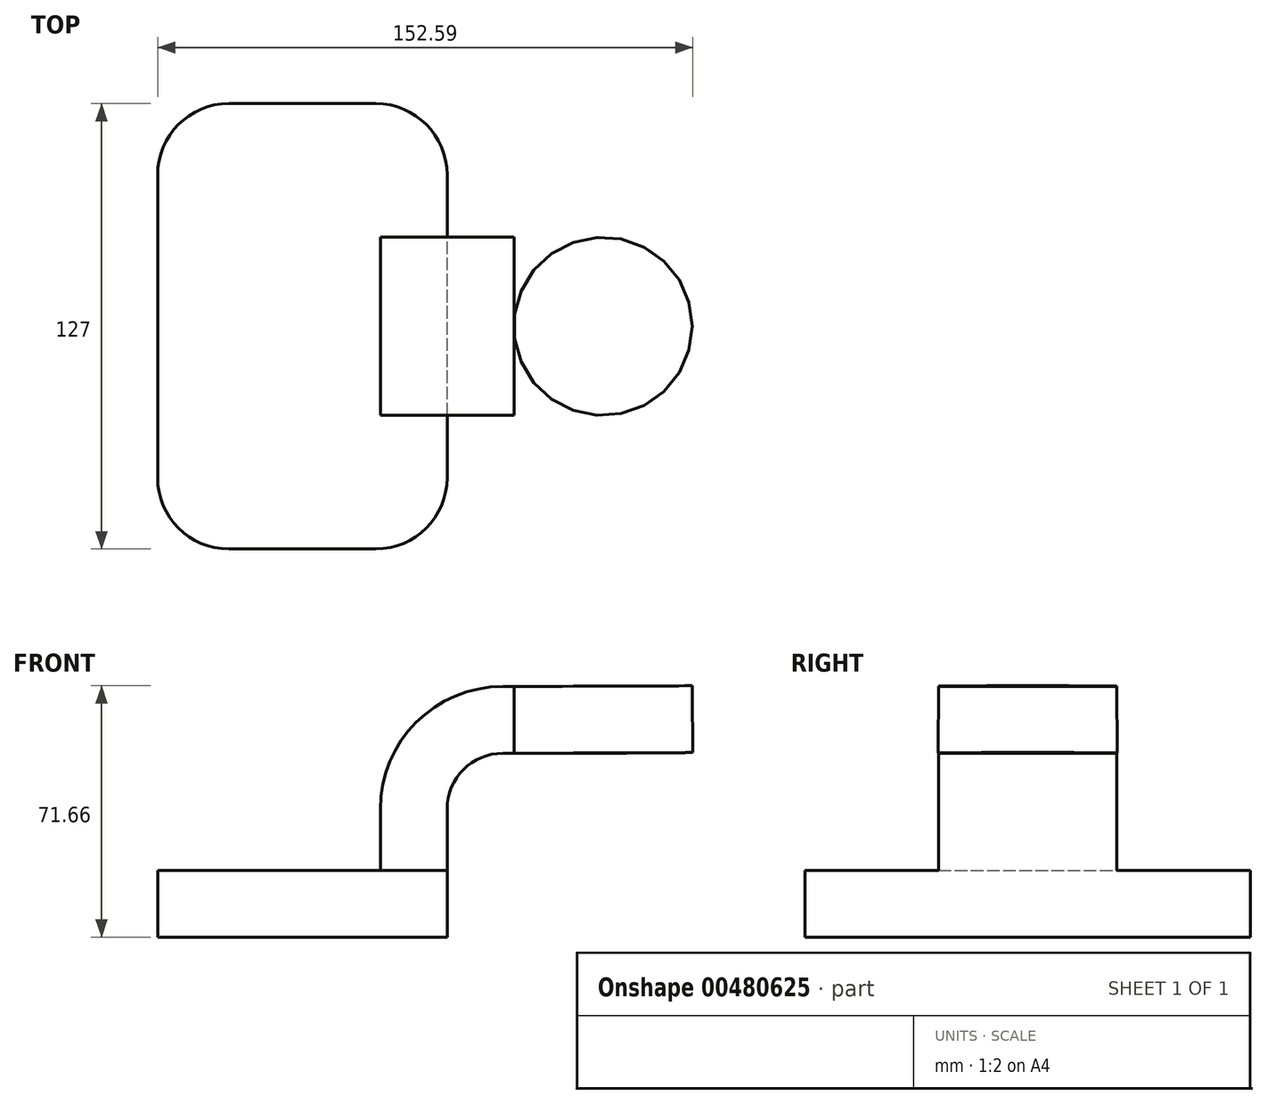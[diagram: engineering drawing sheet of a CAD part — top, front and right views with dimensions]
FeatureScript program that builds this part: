
annotation { "Feature Type Name" : "Feature", "Feature Type Description" : "" }
export const myFeature = defineFeature(function(context is Context, id is Id, definition is map)
    precondition{}
    {
        {
            var Q0;
            Q0=qCreatedBy(makeId("Front.planeOp"),FACE);
            var sketch = newSketch(context, id + "F0", { "sketchPlane" : qUnion([Q0])});
            skLineSegment(sketch, "E0.bottom", {"start": v(-41.28, 9.52) * mm, "end": v(41.27, 9.53) * mm});
            skLineSegment(sketch, "E0.top", {"start": v(-41.28, -9.52) * mm, "end": v(41.28, -9.52) * mm});
            skLineSegment(sketch, "E0.left", {"start": v(-41.28, 9.52) * mm, "end": v(-41.28, -9.53) * mm});
            skLineSegment(sketch, "E0.right", {"start": v(41.27, 9.53) * mm, "end": v(41.28, -9.52) * mm});
            skPoint(sketch, "E0.middle", {"position": v(0, 0) * mm});
            skLineSegment(sketch, "E1.bottom", {"start": v(60.32, 38.1) * mm, "end": v(111.12, 38.1) * mm});
            skLineSegment(sketch, "E1.top", {"start": v(60.32, 66.68) * mm, "end": v(111.12, 66.68) * mm});
            skLineSegment(sketch, "E1.left", {"start": v(60.32, 38.1) * mm, "end": v(60.32, 66.68) * mm});
            skLineSegment(sketch, "E1.right", {"start": v(111.12, 38.1) * mm, "end": v(111.12, 66.68) * mm});
            skPoint(sketch, "E1.middle", {"position": v(85.72, 52.39) * mm});
            skLineSegment(sketch, "E2", {"start": v(41.27, 9.53) * mm, "end": v(41.27, 27) * mm});
            skArc(sketch, "E3", {"start": v(41.27, 27) * mm, "mid": v(45.92, 38.23) * mm, "end": v(57.15, 42.88) * mm});
            skLineSegment(sketch, "E4", {"start": v(57.15, 42.88) * mm, "end": v(85.82, 42.88) * mm});
            skLineSegment(sketch, "E5.0", {"start": v(57.15, 61.93) * mm, "end": v(85.74, 61.93) * mm});
            skArc(sketch, "E5.1", {"start": v(22.22, 27) * mm, "mid": v(32.45, 51.7) * mm, "end": v(57.15, 61.93) * mm});
            skLineSegment(sketch, "E5.2", {"start": v(22.22, 9.53) * mm, "end": v(22.22, 27) * mm});
            skFitSpline(sketch, "E6", {"points": [v(-41.28, 9.52) * mm, v(57.15, 61.93) * mm], "startDerivative": vector(24.3, 107.09) * mm, "endDerivative": vector(112.36, -40.67) * mm});
            skLineSegment(sketch, "E7", {"start": v(85.72, 66.68) * mm, "end": v(85.74, 61.93) * mm});
            skLineSegment(sketch, "E8", {"start": v(85.74, 61.93) * mm, "end": v(85.82, 42.88) * mm});
            skLineSegment(sketch, "E9", {"start": v(85.82, 42.88) * mm, "end": v(85.82, 38.1) * mm});
            skSolve(sketch);
        }
        {
            var Q0;
            Q0=makeQuery(id+"F0.imprint","IMPRINT",FACE,{"disambiguationData":[TD([[makeQuery(id+"F0.imprint","IMPRINT",EDGE,{"derivedFrom":sQuery(id+"F0.wireOp",EDGE,"E0.top")}),1.0]])]});
            extrude(context, id + "F1", {"entities" : qUnion([Q0]), "endBound" : BoundingType.SYMMETRIC, "depth" : 127 * mm});
        }
        {
            var Q0;
            {var subQ1=sQuery(id+"F0.wireOp",EDGE,"E2");Q0=makeQuery(id+"F0.imprint","IMPRINT",FACE,{"disambiguationData":[TD([[makeQuery(id+"F0.imprint","IMPRINT",EDGE,{"derivedFrom":subQ1}),1.0]])]});}
            var Q1;
            {var subQ5=sQuery(id+"F0.wireOp",EDGE,"tLnTp5P4-59iU-ndsa-wNFi-t6ebqTft85pR");Q1=makeQuery(id+"F0.imprint","IMPRINT",FACE,{"disambiguationData":[TD([[makeQuery(id+"F0.imprint","IMPRINT",EDGE,{"derivedFrom":subQ5}),1.0]])]});}
            extrude(context, id + "F2", {"entities" : qUnion([Q0, Q1]), "operationType" : NewBodyOperationType.ADD, "endBound" : BoundingType.SYMMETRIC, "depth" : 50.8 * mm});
        }
        {
            var Q0;
            Q0=makeQuery(id+"F0.imprint","IMPRINT",FACE,{"disambiguationData":[TD([[makeQuery(id+"F0.imprint","IMPRINT",EDGE,{"derivedFrom":sQuery(id+"F0.wireOp",EDGE,"E5.1")}),1.0]])]});
            extrude(context, id + "F3", {"entities" : qUnion([Q0]), "operationType" : NewBodyOperationType.ADD, "endBound" : BoundingType.SYMMETRIC, "depth" : 15.88 * mm});
        }
        {
            var Q0;
            {var subQ5=sQuery(id+"F0.wireOp",EDGE,"E8");Q0=makeQuery(id+"F0.imprint","IMPRINT",FACE,{"disambiguationData":[TD([[makeQuery(id+"F0.imprint","IMPRINT",EDGE,{"derivedFrom":subQ5}),-1.0]])]});}
            var Q1;
            Q1=sQuery(id+"F0.wireOp",EDGE,"E8");
            revolve(context, id + "F4", {"operationType" : NewBodyOperationType.ADD, "entities" : qUnion([Q0]), "axis" : qUnion([Q1]), "revolveType" : RevolveType.FULL});
        }
        {
            var Q0;
            Q0=makeQuery(id+"F1.opExtrude","CAP_EDGE",EDGE,{"disambiguationData":[OSD([sQuery(id+"F0.wireOp",EDGE,"E0.right")])],"isStart":true});
            var Q1;
            Q1=makeQuery(id+"F1.opExtrude","CAP_EDGE",EDGE,{"disambiguationData":[OSD([sQuery(id+"F0.wireOp",EDGE,"E0.left")])],"isStart":true});
            var Q2;
            Q2=makeQuery(id+"F1.opExtrude","CAP_EDGE",EDGE,{"disambiguationData":[OSD([sQuery(id+"F0.wireOp",EDGE,"E0.left")])],"isStart":false});
            var Q3;
            Q3=makeQuery(id+"F1.opExtrude","CAP_EDGE",EDGE,{"disambiguationData":[OSD([sQuery(id+"F0.wireOp",EDGE,"E0.right")])],"isStart":false});
            fillet(context, id + "F5", {"entities" : qUnion([Q0, Q1, Q2, Q3]), "radius" : 20.32 * mm, "tangentPropagation" : true, "allowEdgeOverflow" : false});
        }
    });
